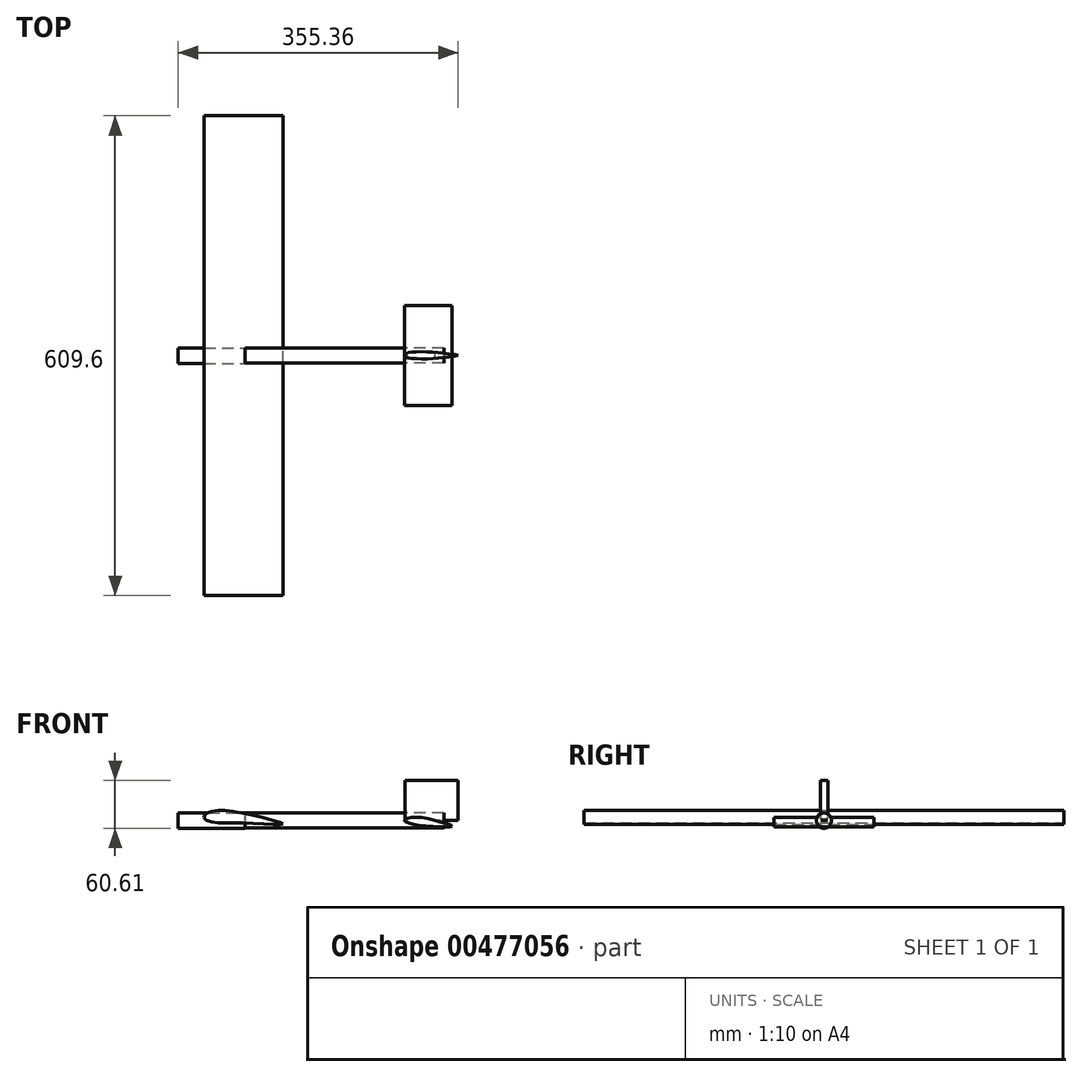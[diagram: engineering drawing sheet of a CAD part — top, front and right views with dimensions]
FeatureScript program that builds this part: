
annotation { "Feature Type Name" : "Feature", "Feature Type Description" : "" }
export const myFeature = defineFeature(function(context is Context, id is Id, definition is map)
    precondition{}
    {
        {
            var Q0;
            Q0=qCreatedBy(makeId("Front.planeOp"),FACE);
            var sketch = newSketch(context, id + "F0", { "sketchPlane" : qUnion([Q0])});
            skFitSpline(sketch, "E0", {"points": [v(48.36, -4.59) * mm, v(4.92, 8.07) * mm, v(-37.29, 12.3) * mm, v(-51.2, 6.83) * mm, v(-51.44, 2.36) * mm, v(-36.05, -2.6) * mm, v(13.1, -3.6) * mm, v(48.36, -4.59) * mm]});
            skSolve(sketch);
        }
        {
            var Q0;
            Q0 = qSketchRegion(id + "F0", true);
            extrude(context, id + "F1", {"entities" : qUnion([Q0]), "depth" : 304.8 * mm});
        }
        {
            var Q0;
            Q0=makeQuery(id+"F1.opExtrude","SWEPT_BODY",BODY,{"disambiguationData":[OSD([sQuery(id+"F0.wireOp",EDGE,"E0")])]});
            var Q1;
            Q1=makeQuery(id+"F1.opExtrude","CAP_FACE",FACE,{"disambiguationData":[OSD([sQuery(id+"F0.wireOp",EDGE,"E0")])],"isStart":true});
            mirror(context, id + "F2", {"operationType" : NewBodyOperationType.ADD, "entities" : qUnion([Q0]), "mirrorPlane" : qUnion([Q1])});
        }
        {
            var Q0;
            Q0=qCreatedBy(makeId("Front.planeOp"),FACE);
            var sketch = newSketch(context, id + "F3", { "sketchPlane" : qUnion([Q0])});
            skFitSpline(sketch, "E1", {"points": [v(263.2, -7.31) * mm, v(241.48, 0) * mm, v(212.25, 3.96) * mm, v(202.65, 0) * mm, v(218.52, -5.64) * mm, v(238.59, -7.76) * mm, v(239.41, -7.8) * mm, v(249, -8.17) * mm, v(263.2, -7.31) * mm]});
            skSolve(sketch);
        }
        {
            var Q0;
            Q0=makeQuery(id+"F3.imprint","IMPRINT",FACE,{"disambiguationData":[TD([[makeQuery(id+"F3.imprint","IMPRINT",EDGE,{"derivedFrom":sQuery(id+"F3.wireOp",EDGE,"E1")}),1.0]])]});
            extrude(context, id + "F4", {"entities" : qUnion([Q0]), "endBound" : BoundingType.SYMMETRIC, "depth" : 127 * mm});
        }
        {
            var Q0;
            Q0=qCreatedBy(makeId("Top.planeOp"),FACE);
            var sketch = newSketch(context, id + "F5", { "sketchPlane" : qUnion([Q0])});
            skFitSpline(sketch, "E2", {"points": [v(270.78, 0) * mm, v(258.32, 2.34) * mm, v(243.2, 3.97) * mm, v(225.99, 4.86) * mm, v(212.34, 4.57) * mm, v(206.11, 3.08) * mm, v(203.44, 0) * mm, v(205.82, -2.7) * mm, v(212.94, -3.74) * mm, v(227.17, -4.33) * mm, v(243.78, -3.44) * mm, v(259.5, -1.51) * mm, v(270.78, 0) * mm]});
            skSolve(sketch);
        }
        {
            var Q0;
            Q0 = qSketchRegion(id + "F5", true);
            extrude(context, id + "F6", {"entities" : qUnion([Q0]), "operationType" : NewBodyOperationType.ADD, "depth" : 50.8 * mm});
        }
        {
            var Q0;
            Q0=qCreatedBy(makeId("Right.planeOp"),FACE);
            var sketch = newSketch(context, id + "F7", { "sketchPlane" : qUnion([Q0])});
            skCircle(sketch, "E3", {"center": v(0, 0) * mm, "radius": 9.49 * mm});
            skSolve(sketch);
        }
        {
            var Q0;
            Q0 = qSketchRegion(id + "F7", true);
            extrude(context, id + "F8", {"entities" : qUnion([Q0]), "depth" : 252.73 * mm});
        }
        {
            var Q0;
            Q0=qCreatedBy(makeId("Right.planeOp"),FACE);
            var sketch = newSketch(context, id + "F9", { "sketchPlane" : qUnion([Q0])});
            skCircle(sketch, "E4", {"center": v(0, 0) * mm, "radius": 9.81 * mm});
            skSolve(sketch);
        }
        {
            var Q0;
            Q0 = qSketchRegion(id + "F9", true);
            extrude(context, id + "F10", {"entities" : qUnion([Q0]), "oppositeDirection" : true, "depth" : 84.58 * mm});
        }
    });
